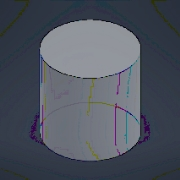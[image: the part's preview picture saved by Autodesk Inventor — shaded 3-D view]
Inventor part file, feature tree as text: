
AUTODESK INVENTOR PART (.ipt)
format: ipt  version: 2024.3 (Build 283343000, 343)  size: 134,656 bytes
history: native  units: mm
features: extrude x1, sketch x1
ambient origin geometry x8: Origin, YZ Plane, XZ Plane, XY Plane, X Axis, Y Axis, Z Axis, Center Point
bodies: Solid1 (feature_tree)
feature tree (2):
  extrude  "Extrusion1"  [1 undecoded]
  sketch  "Sketch1"  dims[d1=25.0mm d2=0.0mm]
note: 1 required parameter value undecoded (feature->parameter linkage not recoverable at this tier; creation-order binding heuristic only, values carry confidence <= 0.55)
